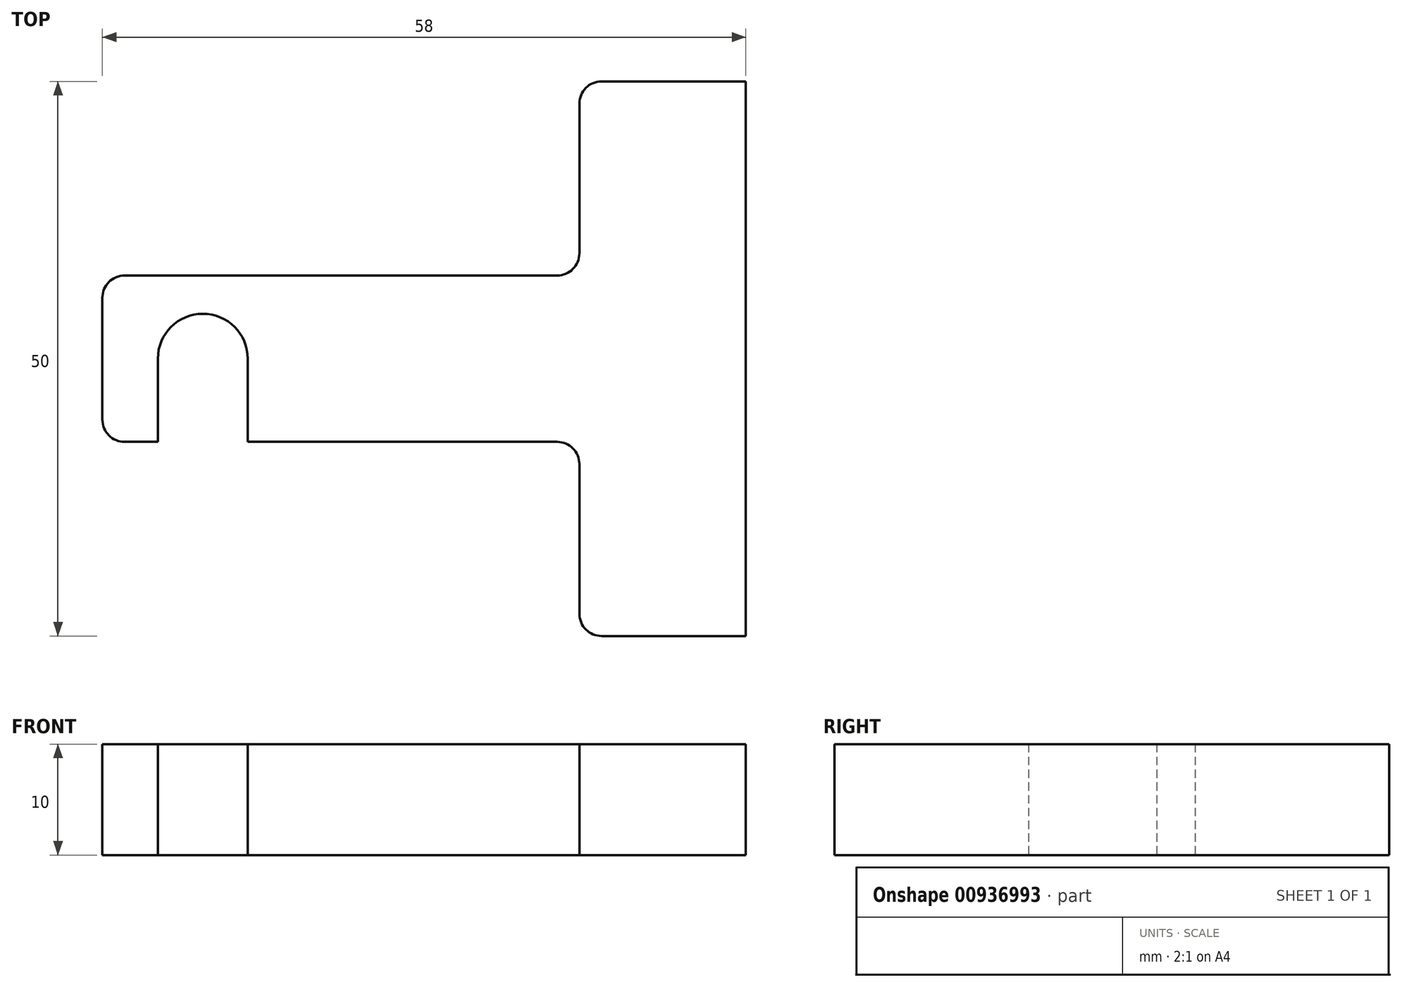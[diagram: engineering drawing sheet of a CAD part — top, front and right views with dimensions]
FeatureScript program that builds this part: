
annotation { "Feature Type Name" : "Feature", "Feature Type Description" : "" }
export const myFeature = defineFeature(function(context is Context, id is Id, definition is map)
    precondition{}
    {
        {
            var Q0;
            Q0=qCreatedBy(makeId("Top.planeOp"),FACE);
            var sketch = newSketch(context, id + "F0", { "sketchPlane" : qUnion([Q0])});
            skLineSegment(sketch, "E0.bottom", {"start": v(19.5, -7.5) * mm, "end": v(-8.4, -7.5) * mm});
            skLineSegment(sketch, "E0.top", {"start": v(19.5, 7.5) * mm, "end": v(-19.5, 7.5) * mm});
            skLineSegment(sketch, "E0.right", {"start": v(-21.5, -5.5) * mm, "end": v(-21.5, 5.5) * mm});
            skPoint(sketch, "E0.middle", {"position": v(0, 0) * mm});
            skLineSegment(sketch, "E1.bottom", {"start": v(23.5, 25) * mm, "end": v(36.5, 25) * mm});
            skLineSegment(sketch, "E1.top", {"start": v(23.5, -25) * mm, "end": v(36.5, -25) * mm});
            skLineSegment(sketch, "E1.left", {"start": v(21.5, 23) * mm, "end": v(21.5, 9.5) * mm});
            skLineSegment(sketch, "E1.right", {"start": v(36.5, 25) * mm, "end": v(36.5, -25) * mm});
            skArc(sketch, "E2", {"start": v(-8.4, 0) * mm, "mid": v(-12.45, 4.05) * mm, "end": v(-16.5, 0) * mm});
            skLineSegment(sketch, "E3.left", {"start": v(-16.5, 0) * mm, "end": v(-16.5, -7.5) * mm});
            skLineSegment(sketch, "E3.right", {"start": v(-8.4, 0) * mm, "end": v(-8.4, -7.5) * mm});
            skLineSegment(sketch, "E4.trimOffspring", {"start": v(-16.5, -7.5) * mm, "end": v(-19.5, -7.5) * mm});
            skLineSegment(sketch, "E5.trimOffspring", {"start": v(21.5, -9.5) * mm, "end": v(21.5, -23) * mm});
            skPoint(sketch, "E6.visualSharp", {"position": v(-21.5, 7.5) * mm});
            skArc(sketch, "E6.filletArc", {"start": v(-19.5, 7.5) * mm, "mid": v(-20.91, 6.91) * mm, "end": v(-21.5, 5.5) * mm});
            skPoint(sketch, "E7.visualSharp", {"position": v(-21.5, -7.5) * mm});
            skArc(sketch, "E7.filletArc", {"start": v(-21.5, -5.5) * mm, "mid": v(-20.91, -6.91) * mm, "end": v(-19.5, -7.5) * mm});
            skPoint(sketch, "E8.visualSharp", {"position": v(21.5, -25) * mm});
            skArc(sketch, "E8.filletArc", {"start": v(21.5, -23) * mm, "mid": v(22.09, -24.41) * mm, "end": v(23.5, -25) * mm});
            skPoint(sketch, "E9.visualSharp", {"position": v(21.5, 25) * mm});
            skArc(sketch, "E9.filletArc", {"start": v(23.5, 25) * mm, "mid": v(22.09, 24.41) * mm, "end": v(21.5, 23) * mm});
            skPoint(sketch, "E10.visualSharp", {"position": v(21.5, 7.5) * mm});
            skArc(sketch, "E10.filletArc", {"start": v(19.5, 7.5) * mm, "mid": v(20.91, 8.09) * mm, "end": v(21.5, 9.5) * mm});
            skPoint(sketch, "E11.visualSharp", {"position": v(21.5, -7.5) * mm});
            skArc(sketch, "E11.filletArc", {"start": v(21.5, -9.5) * mm, "mid": v(20.91, -8.09) * mm, "end": v(19.5, -7.5) * mm});
            skSolve(sketch);
        }
        {
            var Q0;
            Q0 = qSketchRegion(id + "F0", true);
            extrude(context, id + "F1", {"entities" : qUnion([Q0]), "depth" : 10 * mm, "offsetDistance" : 25 * mm});
        }
    });
